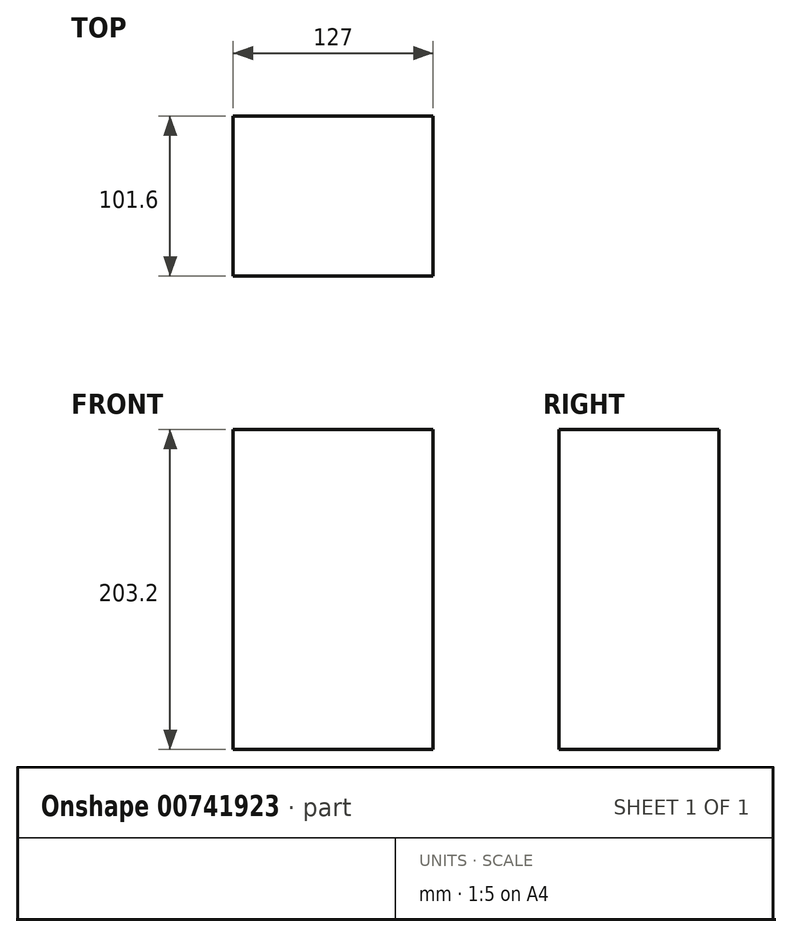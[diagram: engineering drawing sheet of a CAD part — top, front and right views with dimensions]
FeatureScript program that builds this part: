
annotation { "Feature Type Name" : "Feature", "Feature Type Description" : "" }
export const myFeature = defineFeature(function(context is Context, id is Id, definition is map)
    precondition{}
    {
        {
            var Q0;
            Q0=qCreatedBy(makeId("Top.planeOp"),FACE);
            var sketch = newSketch(context, id + "F0", { "sketchPlane" : qUnion([Q0])});
            skLineSegment(sketch, "E0.bottom", {"start": v(0, 0) * mm, "end": v(127, 0) * mm});
            skLineSegment(sketch, "E0.top", {"start": v(0, -101.6) * mm, "end": v(127, -101.6) * mm});
            skLineSegment(sketch, "E0.left", {"start": v(0, 0) * mm, "end": v(0, -101.6) * mm});
            skLineSegment(sketch, "E0.right", {"start": v(127, 0) * mm, "end": v(127, -101.6) * mm});
            skSolve(sketch);
        }
        {
            var Q0;
            Q0 = qSketchRegion(id + "F0", true);
            extrude(context, id + "F1", {"entities" : qUnion([Q0]), "depth" : 203.2 * mm, "offsetDistance" : 25.4 * mm});
        }
    });
